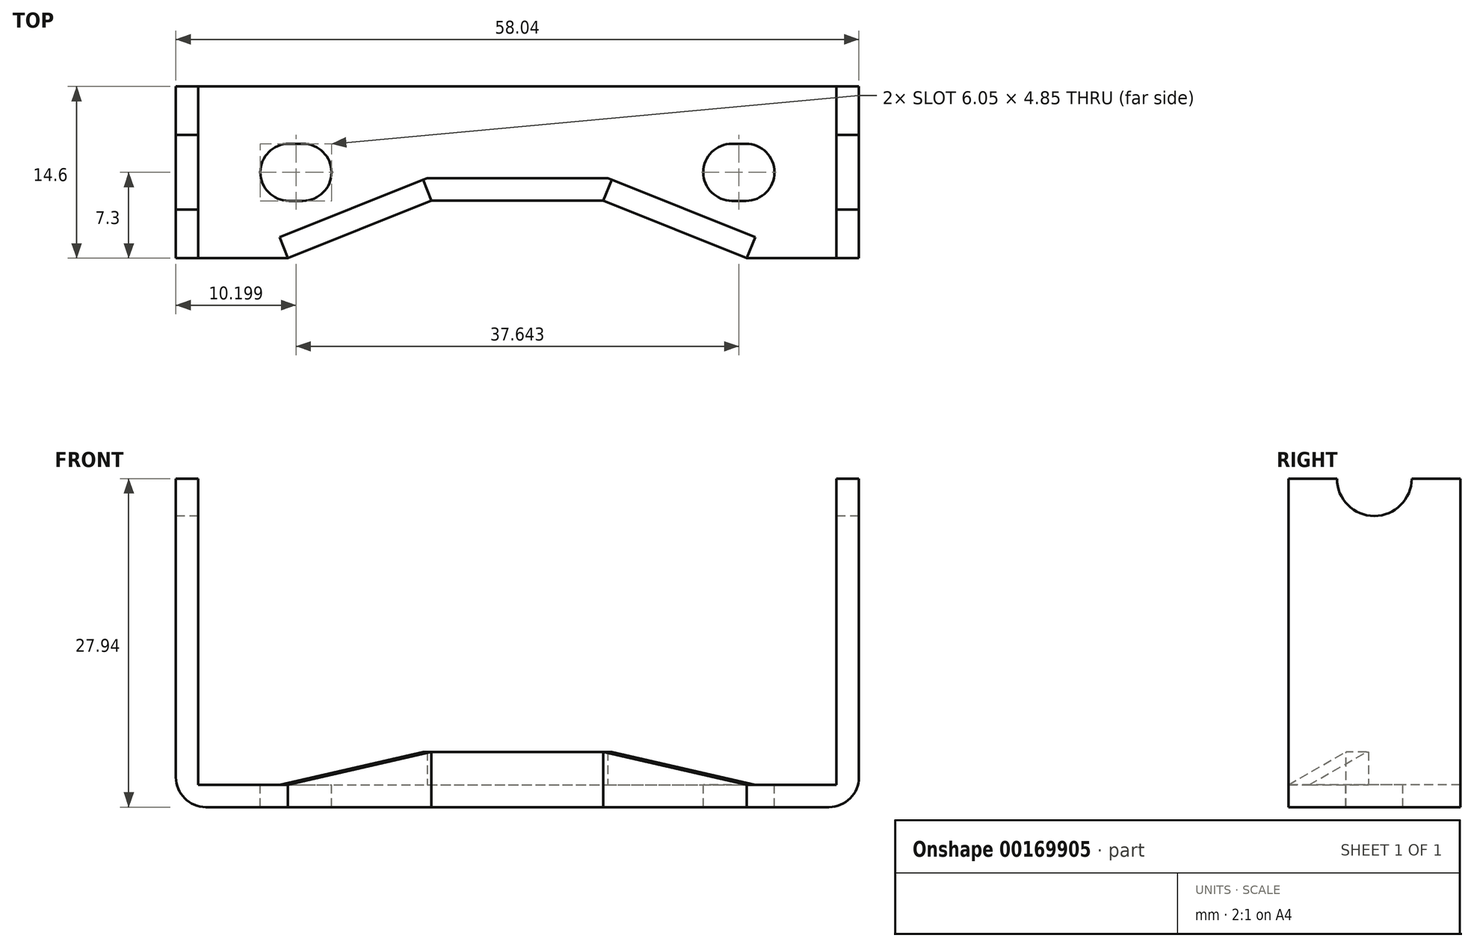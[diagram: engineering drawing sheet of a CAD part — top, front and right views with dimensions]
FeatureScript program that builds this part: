
annotation { "Feature Type Name" : "Feature", "Feature Type Description" : "" }
export const myFeature = defineFeature(function(context is Context, id is Id, definition is map)
    precondition{}
    {
        {
            var Q0;
            Q0=qCreatedBy(makeId("Top.planeOp"),FACE);
            var sketch = newSketch(context, id + "F0", { "sketchPlane" : qUnion([Q0])});
            skLineSegment(sketch, "E0.bottom", {"start": v(-29.02, 7.3) * mm, "end": v(29.02, 7.3) * mm});
            skLineSegment(sketch, "E0.top", {"start": v(-29.02, -7.3) * mm, "end": v(29.02, -7.3) * mm});
            skLineSegment(sketch, "E0.left", {"start": v(-29.02, 7.3) * mm, "end": v(-29.02, -7.3) * mm});
            skLineSegment(sketch, "E0.right", {"start": v(29.02, 7.3) * mm, "end": v(29.02, -7.3) * mm});
            skLineSegment(sketch, "E1", {"start": v(0, 0) * mm, "end": v(0, 7.3) * mm, "construction": true});
            skLineSegment(sketch, "E2", {"start": v(0, 0) * mm, "end": v(-29.02, 0) * mm, "construction": true});
            skSolve(sketch);
        }
        {
            var Q0;
            Q0=makeQuery(id+"F0.imprint","IMPRINT",FACE,{"disambiguationData":[TD([[makeQuery(id+"F0.imprint","IMPRINT",EDGE,{"derivedFrom":sQuery(id+"F0.wireOp",EDGE,"E0.bottom")}),-1.0]])]});
            extrude(context, id + "F1", {"entities" : qUnion([Q0]), "depth" : 1.9 * mm});
        }
        {
            var Q0;
            Q0=makeQuery(id+"F1.opExtrude","CAP_FACE",FACE,{"disambiguationData":[OSD([sQuery(id+"F0.wireOp",EDGE,"E0.bottom"),sQuery(id+"F0.wireOp",EDGE,"E0.top"),sQuery(id+"F0.wireOp",EDGE,"E0.left"),sQuery(id+"F0.wireOp",EDGE,"E0.right")])],"isStart":false});
            var sketch = newSketch(context, id + "F2", { "sketchPlane" : qUnion([Q0])});
            skLineSegment(sketch, "E3.bottom", {"start": v(-29.02, 7.3) * mm, "end": v(-27.11, 7.3) * mm});
            skLineSegment(sketch, "E3.top", {"start": v(-29.02, -7.3) * mm, "end": v(-27.11, -7.3) * mm});
            skLineSegment(sketch, "E3.left", {"start": v(-29.02, 7.3) * mm, "end": v(-29.02, -7.3) * mm});
            skLineSegment(sketch, "E3.right", {"start": v(-27.11, 7.3) * mm, "end": v(-27.11, -7.3) * mm});
            skLineSegment(sketch, "E4.bottom", {"start": v(29.02, 7.3) * mm, "end": v(27.11, 7.3) * mm});
            skLineSegment(sketch, "E4.top", {"start": v(29.02, -7.3) * mm, "end": v(27.11, -7.3) * mm});
            skLineSegment(sketch, "E4.left", {"start": v(29.02, 7.3) * mm, "end": v(29.02, -7.3) * mm});
            skLineSegment(sketch, "E4.right", {"start": v(27.11, 7.3) * mm, "end": v(27.11, -7.3) * mm});
            skSolve(sketch);
        }
        {
            var Q0;
            Q0=makeQuery(id+"F2.imprint","IMPRINT",FACE,{"disambiguationData":[TD([[makeQuery(id+"F2.imprint","IMPRINT",EDGE,{"derivedFrom":sQuery(id+"F2.wireOp",EDGE,"E3.bottom")}),-1.0]])]});
            var Q1;
            Q1=makeQuery(id+"F2.imprint","IMPRINT",FACE,{"disambiguationData":[TD([[makeQuery(id+"F2.imprint","IMPRINT",EDGE,{"derivedFrom":sQuery(id+"F2.wireOp",EDGE,"E4.bottom")}),-1.0]])]});
            extrude(context, id + "F3", {"entities" : qUnion([Q0, Q1]), "operationType" : NewBodyOperationType.ADD, "depth" : 26.04 * mm});
        }
        {
            var Q0;
            Q0=makeQuery(id+"F1.opExtrude","CAP_EDGE",EDGE,{"disambiguationData":[OSD([sQuery(id+"F0.wireOp",EDGE,"E0.left")])],"isStart":true});
            var Q1;
            Q1=makeQuery(id+"F1.opExtrude","CAP_EDGE",EDGE,{"disambiguationData":[OSD([sQuery(id+"F0.wireOp",EDGE,"E0.right")])],"isStart":true});
            var Q2;
            Q2=makeQuery(id+"F3.opExtrude","CAP_EDGE",EDGE,{"disambiguationData":[OSD([sQuery(id+"F2.wireOp",EDGE,"E4.right")])],"isStart":true});
            var Q3;
            Q3=makeQuery(id+"F3.opExtrude","CAP_EDGE",EDGE,{"disambiguationData":[OSD([sQuery(id+"F2.wireOp",EDGE,"E3.right")])],"isStart":true});
            fillet(context, id + "F4", {"entities" : qUnion([Q0, Q1, Q2, Q3]), "radius" : 2.54 * mm, "tangentPropagation" : true, "allowEdgeOverflow" : false});
        }
        {
            var Q0;
            Q0=makeQuery(id+"F3.boolean.opBoolean","MERGE",FACE,{"derivedFrom":[makeQuery(id+"F1.opExtrude","SWEPT_FACE",FACE,{"disambiguationData":[OSD([sQuery(id+"F0.wireOp",EDGE,"E0.left")])]}),makeQuery(id+"F3.opExtrude","SWEPT_FACE",FACE,{"disambiguationData":[OSD([sQuery(id+"F2.wireOp",EDGE,"E3.left")])]})]});
            var sketch = newSketch(context, id + "F5", { "sketchPlane" : qUnion([Q0])});
            skLineSegment(sketch, "E5", {"start": v(-7.3, 27.94) * mm, "end": v(-3.18, 27.94) * mm});
            skLineSegment(sketch, "E6", {"start": v(7.3, 27.94) * mm, "end": v(3.17, 27.94) * mm});
            skArc(sketch, "E7", {"start": v(-3.18, 27.94) * mm, "mid": v(0, 24.77) * mm, "end": v(3.17, 27.94) * mm});
            skSolve(sketch);
        }
        {
            var Q0;
            {var subQ0=sQuery(id+"F5.wireOp",EDGE,"E7");Q0=makeQuery(id+"F5.imprint","IMPRINT",FACE,{"disambiguationData":[TD([[makeQuery(id+"F5.imprint","IMPRINT",EDGE,{"derivedFrom":subQ0}),1.0]])]});}
            extrude(context, id + "F6", {"entities" : qUnion([Q0]), "operationType" : NewBodyOperationType.REMOVE, "endBound" : BoundingType.THROUGH_ALL, "oppositeDirection" : true, "depth" : 25.4 * mm});
        }
        {
            var Q0;
            Q0=makeQuery(id+"F1.opExtrude","CAP_FACE",FACE,{"disambiguationData":[OSD([sQuery(id+"F0.wireOp",EDGE,"E0.bottom"),sQuery(id+"F0.wireOp",EDGE,"E0.top"),sQuery(id+"F0.wireOp",EDGE,"E0.left"),sQuery(id+"F0.wireOp",EDGE,"E0.right")])],"isStart":false});
            var sketch = newSketch(context, id + "F7", { "sketchPlane" : qUnion([Q0])});
            skLineSegment(sketch, "E8.bottom", {"start": v(-19.42, 2.43) * mm, "end": v(-18.22, 2.43) * mm});
            skLineSegment(sketch, "E8.top", {"start": v(-19.42, -2.43) * mm, "end": v(-18.22, -2.43) * mm});
            skArc(sketch, "E9", {"start": v(-19.42, 2.43) * mm, "mid": v(-21.84, 0) * mm, "end": v(-19.42, -2.43) * mm});
            skArc(sketch, "E10", {"start": v(-18.22, -2.43) * mm, "mid": v(-15.8, 0) * mm, "end": v(-18.22, 2.43) * mm});
            skLineSegment(sketch, "E11.bottom", {"start": v(18.22, 2.43) * mm, "end": v(19.42, 2.43) * mm});
            skLineSegment(sketch, "E11.top", {"start": v(18.22, -2.43) * mm, "end": v(19.42, -2.43) * mm});
            skArc(sketch, "E12", {"start": v(18.22, 2.43) * mm, "mid": v(15.8, 0) * mm, "end": v(18.22, -2.43) * mm});
            skArc(sketch, "E13", {"start": v(19.42, -2.43) * mm, "mid": v(21.84, 0) * mm, "end": v(19.42, 2.43) * mm});
            skLineSegment(sketch, "E14", {"start": v(0, 7.3) * mm, "end": v(0, -7.3) * mm, "construction": true});
            skSolve(sketch);
        }
        {
            var Q0;
            Q0=makeQuery(id+"F7.imprint","IMPRINT",FACE,{"disambiguationData":[TD([[makeQuery(id+"F7.imprint","IMPRINT",EDGE,{"derivedFrom":sQuery(id+"F7.wireOp",EDGE,"E8.bottom")}),-1.0]])]});
            var Q1;
            Q1=makeQuery(id+"F7.imprint","IMPRINT",FACE,{"disambiguationData":[TD([[makeQuery(id+"F7.imprint","IMPRINT",EDGE,{"derivedFrom":sQuery(id+"F7.wireOp",EDGE,"E11.bottom")}),-1.0]])]});
            extrude(context, id + "F8", {"entities" : qUnion([Q0, Q1]), "operationType" : NewBodyOperationType.REMOVE, "endBound" : BoundingType.UP_TO_NEXT, "oppositeDirection" : true, "depth" : 25.4 * mm});
        }
        {
            var Q0;
            Q0=makeQuery(id+"F1.opExtrude","CAP_FACE",FACE,{"disambiguationData":[OSD([sQuery(id+"F0.wireOp",EDGE,"E0.bottom"),sQuery(id+"F0.wireOp",EDGE,"E0.top"),sQuery(id+"F0.wireOp",EDGE,"E0.left"),sQuery(id+"F0.wireOp",EDGE,"E0.right")])],"isStart":false});
            var sketch = newSketch(context, id + "F9", { "sketchPlane" : qUnion([Q0])});
            skLineSegment(sketch, "E15", {"start": v(-24.57, -7.3) * mm, "end": v(-19.5, -7.3) * mm});
            skLineSegment(sketch, "E16", {"start": v(-19.5, -7.3) * mm, "end": v(-7.3, -2.41) * mm});
            skLineSegment(sketch, "E17", {"start": v(-7.3, -2.41) * mm, "end": v(7.3, -2.41) * mm});
            skLineSegment(sketch, "E18", {"start": v(7.3, -2.41) * mm, "end": v(19.5, -7.3) * mm});
            skLineSegment(sketch, "E19", {"start": v(19.5, -7.3) * mm, "end": v(24.57, -7.3) * mm});
            skLineSegment(sketch, "E20", {"start": v(0, 7.3) * mm, "end": v(0, -7.3) * mm, "construction": true});
            skSolve(sketch);
        }
        {
            var Q0;
            {var subQ0=sQuery(id+"F9.wireOp",EDGE,"E16");Q0=makeQuery(id+"F9.imprint","IMPRINT",FACE,{"disambiguationData":[TD([[makeQuery(id+"F9.imprint","IMPRINT",EDGE,{"derivedFrom":subQ0}),-1.0]])]});}
            extrude(context, id + "F10", {"entities" : qUnion([Q0]), "operationType" : NewBodyOperationType.REMOVE, "endBound" : BoundingType.UP_TO_NEXT, "oppositeDirection" : true, "depth" : 25.4 * mm});
        }
        {
            var Q0;
            Q0=makeQuery(id+"F1.opExtrude","CAP_FACE",FACE,{"disambiguationData":[OSD([sQuery(id+"F0.wireOp",EDGE,"E0.bottom"),sQuery(id+"F0.wireOp",EDGE,"E0.top"),sQuery(id+"F0.wireOp",EDGE,"E0.left"),sQuery(id+"F0.wireOp",EDGE,"E0.right")])],"isStart":false});
            var sketch = newSketch(context, id + "F11", { "sketchPlane" : qUnion([Q0])});
            skLineSegment(sketch, "E21", {"start": v(-19.5, -7.3) * mm, "end": v(-7.3, -2.41) * mm});
            skLineSegment(sketch, "E22", {"start": v(-7.3, -2.41) * mm, "end": v(7.3, -2.41) * mm});
            skLineSegment(sketch, "E23", {"start": v(7.3, -2.41) * mm, "end": v(19.5, -7.3) * mm});
            skLineSegment(sketch, "E24.0", {"start": v(7.67, -0.5) * mm, "end": v(20.2, -5.53) * mm});
            skLineSegment(sketch, "E24.1", {"start": v(-7.67, -0.5) * mm, "end": v(7.67, -0.5) * mm});
            skLineSegment(sketch, "E24.2", {"start": v(-20.2, -5.53) * mm, "end": v(-7.67, -0.5) * mm});
            skLineSegment(sketch, "E25", {"start": v(-19.5, -7.3) * mm, "end": v(-20.2, -5.53) * mm});
            skLineSegment(sketch, "E26", {"start": v(19.5, -7.3) * mm, "end": v(20.2, -5.53) * mm});
            skSolve(sketch);
        }
        {
            var Q0;
            Q0=makeQuery(id+"F11.imprint","IMPRINT",FACE,{"disambiguationData":[TD([[makeQuery(id+"F11.imprint","IMPRINT",EDGE,{"derivedFrom":sQuery(id+"F11.wireOp",EDGE,"E21")}),1.0]])]});
            extrude(context, id + "F12", {"entities" : qUnion([Q0]), "operationType" : NewBodyOperationType.ADD, "depth" : 2.8 * mm});
        }
        {
            var Q0;
            Q0=makeQuery(id+"F12.boolean.opBoolean","MERGE",FACE,{"derivedFrom":[makeQuery(id+"F10.boolean.opBoolean","COPY",FACE,{"derivedFrom":makeQuery(id+"F10.opExtrude","SWEPT_FACE",FACE,{"disambiguationData":[OSD([sQuery(id+"F9.wireOp",EDGE,"E16")])]})}),makeQuery(id+"F12.opExtrude","SWEPT_FACE",FACE,{"disambiguationData":[OSD([sQuery(id+"F11.wireOp",EDGE,"E21")])]})]});
            var sketch = newSketch(context, id + "F13", { "sketchPlane" : qUnion([Q0])});
            skLineSegment(sketch, "E27", {"start": v(-20.81, 1.9) * mm, "end": v(-7.68, 4.7) * mm});
            skLineSegment(sketch, "E28", {"start": v(-7.68, 4.7) * mm, "end": v(-7.68, 1.9) * mm});
            skLineSegment(sketch, "E29", {"start": v(-7.68, 1.9) * mm, "end": v(-20.81, 1.9) * mm});
            skSolve(sketch);
        }
        {
            var Q0;
            Q0=makeQuery(id+"F13.imprint","IMPRINT",FACE,{"disambiguationData":[TD([[makeQuery(id+"F13.imprint","IMPRINT",EDGE,{"derivedFrom":sQuery(id+"F13.wireOp",EDGE,"E27")}),1.0]])]});
            extrude(context, id + "F14", {"entities" : qUnion([Q0]), "operationType" : NewBodyOperationType.REMOVE, "endBound" : BoundingType.UP_TO_NEXT, "oppositeDirection" : true, "depth" : 25.4 * mm});
        }
        {
            var Q0;
            Q0=makeQuery(id+"F12.boolean.opBoolean","MERGE",FACE,{"derivedFrom":[makeQuery(id+"F10.boolean.opBoolean","COPY",FACE,{"derivedFrom":makeQuery(id+"F10.opExtrude","SWEPT_FACE",FACE,{"disambiguationData":[OSD([sQuery(id+"F9.wireOp",EDGE,"E18")])]})}),makeQuery(id+"F12.opExtrude","SWEPT_FACE",FACE,{"disambiguationData":[OSD([sQuery(id+"F11.wireOp",EDGE,"E23")])]})]});
            var sketch = newSketch(context, id + "F15", { "sketchPlane" : qUnion([Q0])});
            skLineSegment(sketch, "E30", {"start": v(20.81, 1.9) * mm, "end": v(7.68, 4.7) * mm});
            skLineSegment(sketch, "E31", {"start": v(7.68, 4.7) * mm, "end": v(7.68, 1.9) * mm});
            skLineSegment(sketch, "E32", {"start": v(7.68, 1.9) * mm, "end": v(20.81, 1.9) * mm});
            skSolve(sketch);
        }
        {
            var Q0;
            Q0=makeQuery(id+"F15.imprint","IMPRINT",FACE,{"disambiguationData":[TD([[makeQuery(id+"F15.imprint","IMPRINT",EDGE,{"derivedFrom":sQuery(id+"F15.wireOp",EDGE,"E30")}),-1.0]])]});
            extrude(context, id + "F16", {"entities" : qUnion([Q0]), "operationType" : NewBodyOperationType.REMOVE, "endBound" : BoundingType.UP_TO_NEXT, "oppositeDirection" : true, "depth" : 25.4 * mm});
        }
    });
